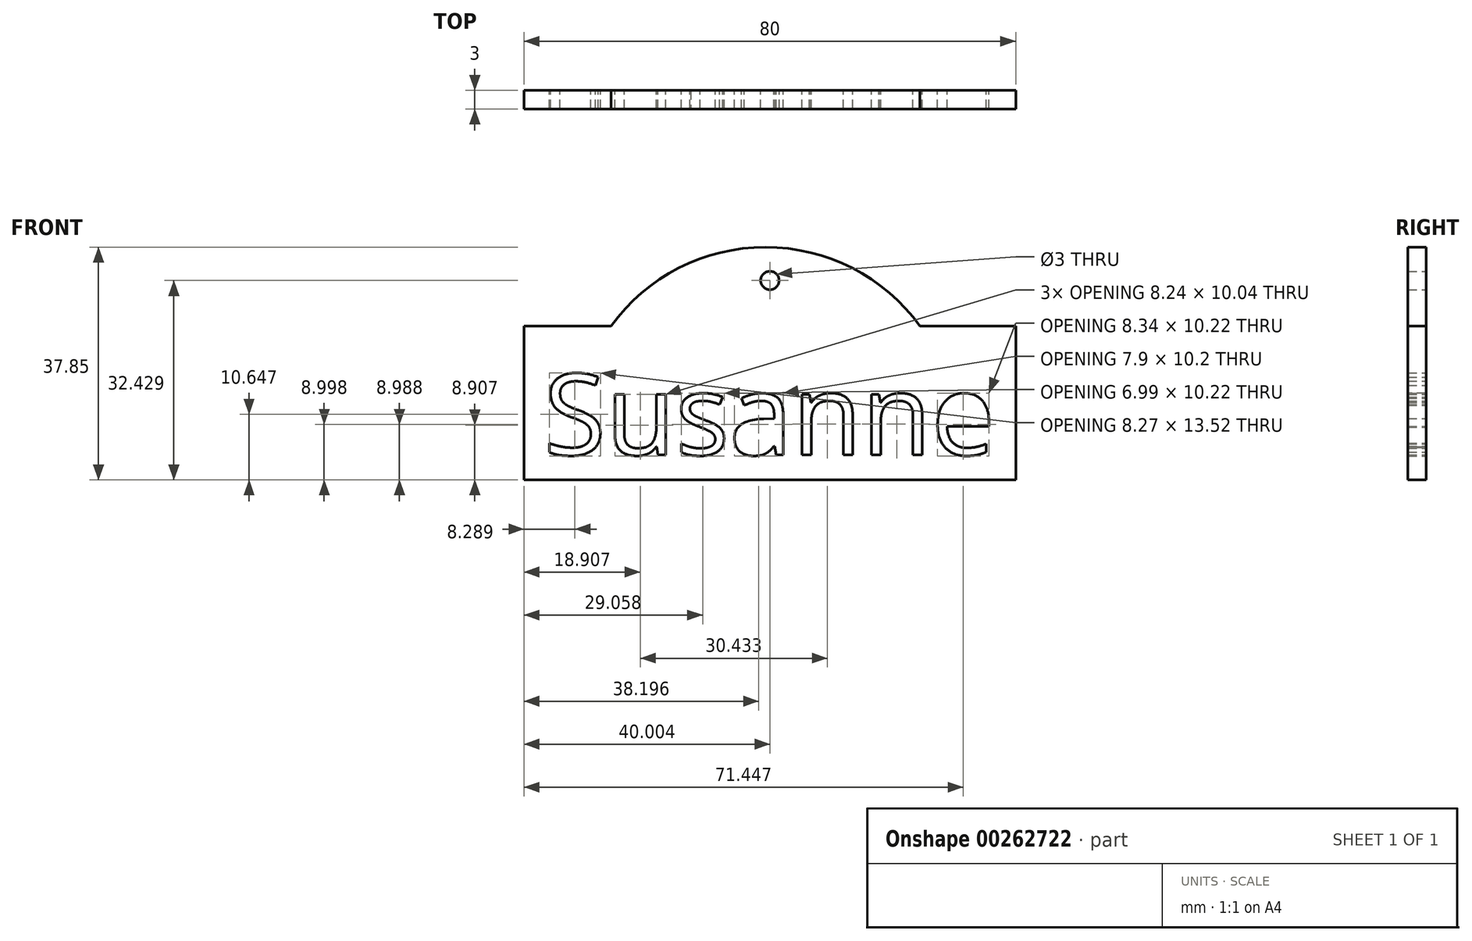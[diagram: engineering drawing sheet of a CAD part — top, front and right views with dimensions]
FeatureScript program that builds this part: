
annotation { "Feature Type Name" : "Feature", "Feature Type Description" : "" }
export const myFeature = defineFeature(function(context is Context, id is Id, definition is map)
    precondition{}
    {
        {
            var Q0;
            Q0=qCreatedBy(makeId("Front.planeOp"),FACE);
            var sketch = newSketch(context, id + "F0", { "sketchPlane" : qUnion([Q0])});
            skLineSegment(sketch, "E0.bottom", {"start": v(-76.35, 50.11) * mm, "end": v(3.65, 50.11) * mm});
            skLineSegment(sketch, "E0.top", {"start": v(-76.35, 25.11) * mm, "end": v(3.65, 25.11) * mm});
            skLineSegment(sketch, "E0.left", {"start": v(-76.35, 50.11) * mm, "end": v(-76.35, 25.11) * mm});
            skLineSegment(sketch, "E0.right", {"start": v(3.65, 50.11) * mm, "end": v(3.65, 25.11) * mm});
            skText(sketch, "E1", { "text": "Susanne\n", "fontName": "OpenSans-Regular.ttf"});
            skArc(sketch, "E2", {"start": v(-11.93, 50.11) * mm, "mid": v(-37.07, 62.96) * mm, "end": v(-62.2, 50.11) * mm});
            skCircle(sketch, "E3", {"center": v(-36.35, 57.54) * mm, "radius": 1.5 * mm});
            skPoint(sketch, "E4", {"position": v(-36.35, 50.11) * mm});
            skPoint(sketch, "E5", {"position": v(-43.42, 62.3) * mm});
            skPoint(sketch, "E6", {"position": v(-36.35, 62.95) * mm});
            const initialGuessF0  = {"E1": [-0.07315, 0.02918, 1, 0, 0.01326]};
            skSetInitialGuess(sketch, initialGuessF0);
            skSolve(sketch);
        }
        {
            var Q0;
            Q0 = qSketchRegion(id + "F0", true);
            extrude(context, id + "F1", {"entities" : qUnion([Q0]), "depth" : 3 * mm});
        }
    });
